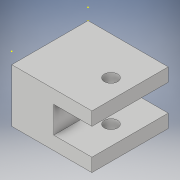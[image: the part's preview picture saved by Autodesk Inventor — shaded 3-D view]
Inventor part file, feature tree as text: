
AUTODESK INVENTOR PART (.ipt)
format: ipt  version: 2017 (Build 210142000, 142)  size: 145,920 bytes
history: native  units: in
note: dims shown in document units (in); Inventor stores cm internally (conversion verified against a paired STEP export)
features: sketch x10, extrude x6
ambient origin geometry x8: Origin, YZ Plane, XZ Plane, XY Plane, X Axis, Y Axis, Z Axis, Center Point
bodies: Solid1 (feature_tree)
feature tree (16):
  extrude  "Extrusion1"  Depth=0.8268in
  sketch  "Sketch2"  dims[d2=0.2559in d3=0.3937in]
  sketch  "Sketch3"  dims[d4=0.2756in d5=90.0deg]
  extrude  "Extrusion2"  Depth=0.3937in
  sketch  "Sketch5"  dims[d9=0.3937in d10=0.3937in]
  extrude  "Extrusion3"  TaperAngle=90.0deg  [1 undecoded]
  extrude  "Extrusion4"  Depth=0.7874in
  sketch  "Sketch8"  dims[d17=0.4331in]
  extrude  "Extrusion5"  Depth=0.3937in
  extrude  "Extrusion6"  Depth=0.4331in TaperAngle=0.0deg
  sketch  "Sketch1"  dims[d0=0.7874in d1=0.8268in]
  sketch  "Sketch4"  dims[d6=0.7874in d7=0.0in d8=0.2165in]
  sketch  "Sketch6"  dims[d11=0.4331in d12=0.0in d13=0.1181in d14=0.0in]
  sketch  "Sketch7"  dims[d15=0.1181in d16=0.0in]
  sketch  "Sketch9"  dims[d18=0.1378in]
  sketch  "Sketch10"  dims[d19=0.1969in d20=0.3937in d21=0.1378in d22=0.0in d23=0.1378in d24=0.1969in d25=0.3937in d26=0.1378in d27=0.0in]
note: 1 required parameter value undecoded (feature->parameter linkage not recoverable at this tier; creation-order binding heuristic only, values carry confidence <= 0.55)
